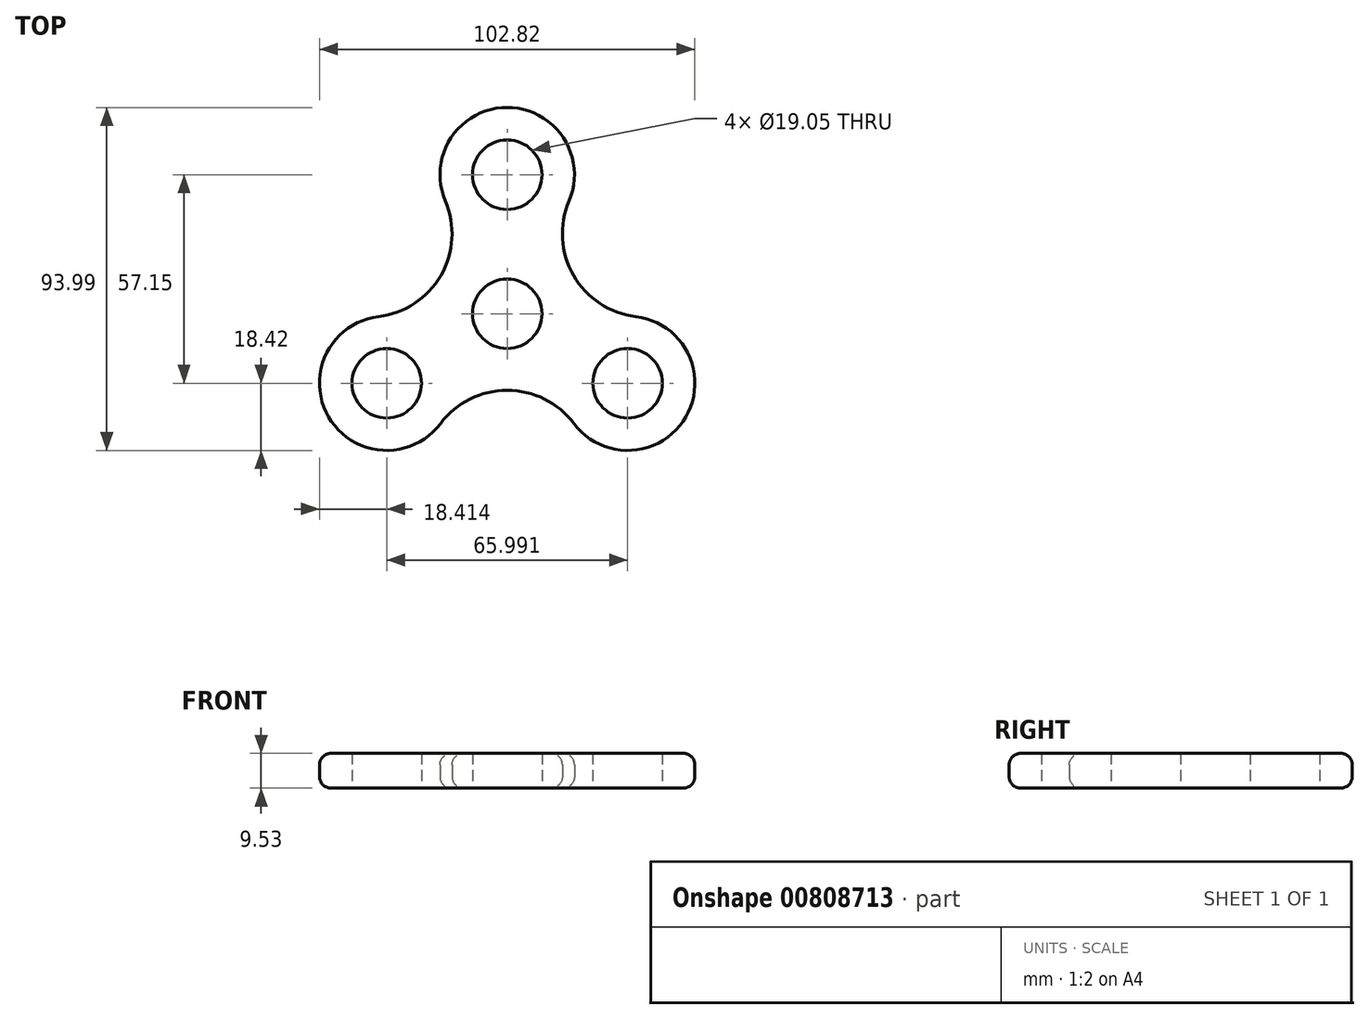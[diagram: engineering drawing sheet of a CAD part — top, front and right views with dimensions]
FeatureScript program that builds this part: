
annotation { "Feature Type Name" : "Feature", "Feature Type Description" : "" }
export const myFeature = defineFeature(function(context is Context, id is Id, definition is map)
    precondition{}
    {
        {
            var Q0;
            Q0=qCreatedBy(makeId("Top.planeOp"),FACE);
            var sketch = newSketch(context, id + "F0", { "sketchPlane" : qUnion([Q0])});
            skCircle(sketch, "E0", {"center": v(0, 38.1) * mm, "radius": 9.53 * mm});
            skCircle(sketch, "E1", {"center": v(0, 0) * mm, "radius": 9.53 * mm});
            skCircle(sketch, "E2", {"center": v(-33, -19.05) * mm, "radius": 9.53 * mm});
            skCircle(sketch, "E3", {"center": v(33, -19.05) * mm, "radius": 9.53 * mm});
            skLineSegment(sketch, "E4", {"start": v(0, 38.1) * mm, "end": v(0, 0) * mm, "construction": true});
            skLineSegment(sketch, "E5", {"start": v(-33, -19.05) * mm, "end": v(0, 0) * mm, "construction": true});
            skLineSegment(sketch, "E6", {"start": v(33, -19.05) * mm, "end": v(0, 0) * mm, "construction": true});
            skArc(sketch, "E7", {"start": v(16.94, 30.88) * mm, "mid": v(0, 56.51) * mm, "end": v(-16.94, 30.88) * mm});
            skArc(sketch, "E8", {"start": v(18.27, -30.11) * mm, "mid": v(48.94, -28.26) * mm, "end": v(35.22, -0.77) * mm});
            skArc(sketch, "E9", {"start": v(-35.22, -0.77) * mm, "mid": v(-48.94, -28.26) * mm, "end": v(-18.27, -30.11) * mm});
            skArc(sketch, "E10", {"start": v(-35.22, -0.77) * mm, "mid": v(-18.18, 10.5) * mm, "end": v(-16.94, 30.88) * mm});
            skArc(sketch, "E11", {"start": v(16.94, 30.88) * mm, "mid": v(18.18, 10.5) * mm, "end": v(35.22, -0.77) * mm});
            skArc(sketch, "E12", {"start": v(18.27, -30.11) * mm, "mid": v(0, -20.99) * mm, "end": v(-18.27, -30.11) * mm});
            skSolve(sketch);
        }
        {
            var Q0;
            Q0=makeQuery(id+"F0.imprint","IMPRINT",FACE,{"disambiguationData":[TD([[makeQuery(id+"F0.imprint","IMPRINT",EDGE,{"derivedFrom":sQuery(id+"F0.wireOp",EDGE,"E0")}),-1.0]])]});
            extrude(context, id + "F1", {"entities" : qUnion([Q0]), "depth" : 9.52 * mm, "offsetDistance" : 25.4 * mm});
        }
        {
            var Q0;
            Q0=makeQuery(id+"F1.opExtrude","CAP_EDGE",EDGE,{"disambiguationData":[OSD([sQuery(id+"F0.wireOp",EDGE,"E10")])],"isStart":false});
            var Q1;
            Q1=makeQuery(id+"F1.opExtrude","CAP_EDGE",EDGE,{"disambiguationData":[OSD([sQuery(id+"F0.wireOp",EDGE,"E11")])],"isStart":true});
            fillet(context, id + "F2", {"entities" : qUnion([Q0, Q1]), "radius" : 3.17 * mm, "tangentPropagation" : true, "allowEdgeOverflow" : false});
        }
    });
